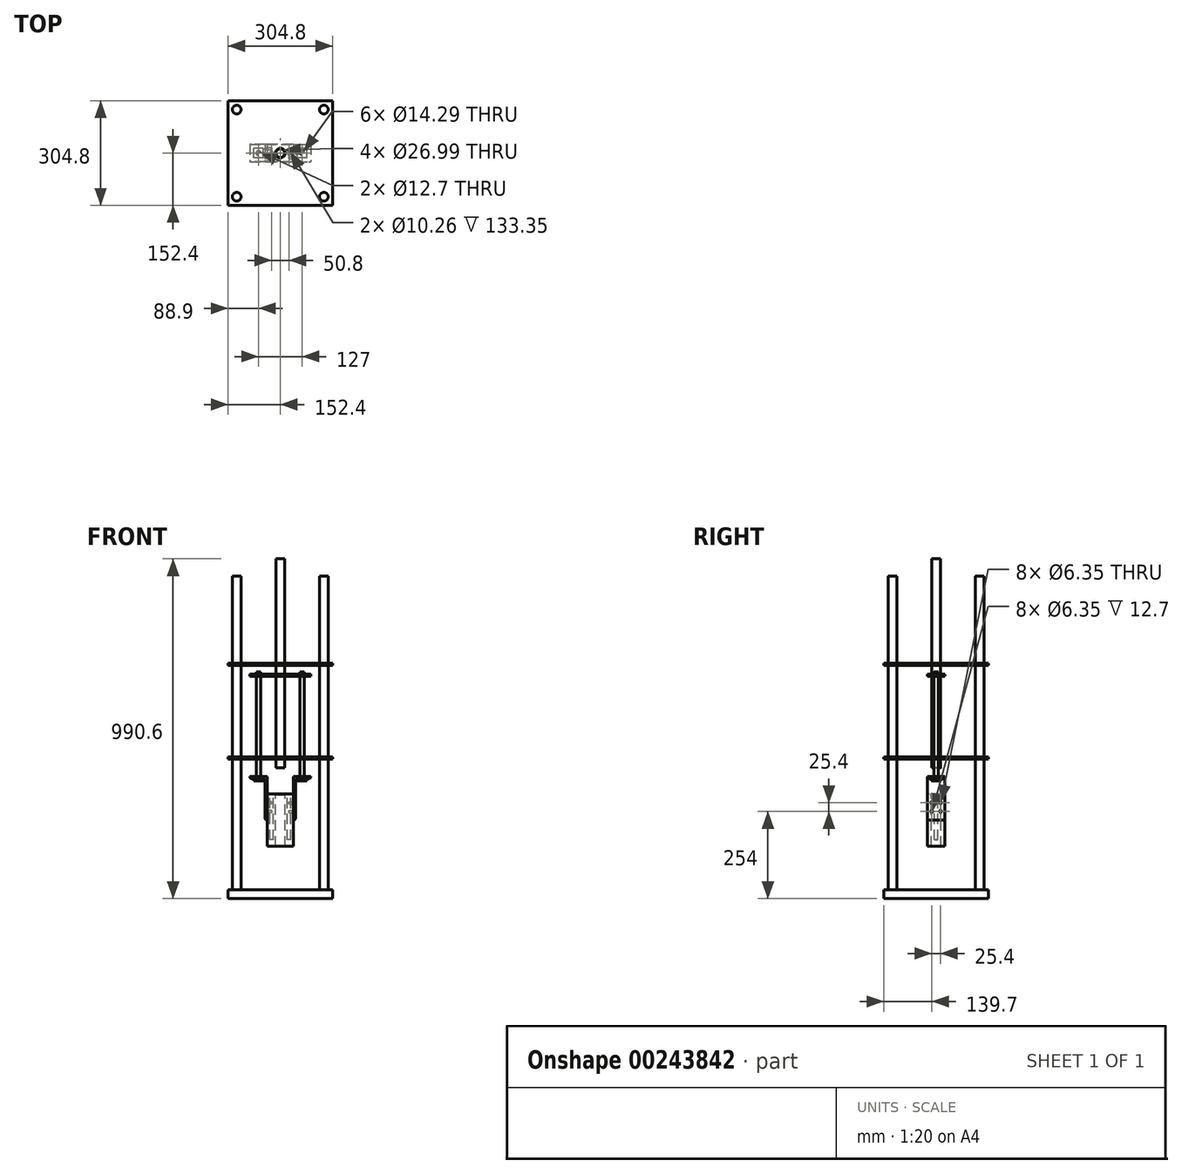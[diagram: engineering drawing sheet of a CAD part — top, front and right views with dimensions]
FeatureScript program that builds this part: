
annotation { "Feature Type Name" : "Feature", "Feature Type Description" : "" }
export const myFeature = defineFeature(function(context is Context, id is Id, definition is map)
    precondition{}
    {
        {
            var Q0;
            Q0=qCreatedBy(makeId("Top.planeOp"),FACE);
            var sketch = newSketch(context, id + "F0", { "sketchPlane" : qUnion([Q0])});
            skPoint(sketch, "E0.middle", {"position": v(0, 0) * mm});
            skLineSegment(sketch, "E1.bottom", {"start": v(152.4, 152.4) * mm, "end": v(-152.4, 152.4) * mm});
            skLineSegment(sketch, "E1.top", {"start": v(152.4, -152.4) * mm, "end": v(-152.4, -152.4) * mm});
            skLineSegment(sketch, "E1.left", {"start": v(152.4, 152.4) * mm, "end": v(152.4, -152.4) * mm});
            skLineSegment(sketch, "E1.right", {"start": v(-152.4, 152.4) * mm, "end": v(-152.4, -152.4) * mm});
            skSolve(sketch);
        }
        {
            var Q0;
            Q0 = qSketchRegion(id + "F0", true);
            extrude(context, id + "F1", {"entities" : qUnion([Q0]), "oppositeDirection" : true, "depth" : 25.4 * mm});
        }
        {
            var Q0;
            Q0=makeQuery(id+"F1.opExtrude","CAP_FACE",FACE,{"disambiguationData":[OSD([sQuery(id+"F0.wireOp",EDGE,"E1.bottom"),sQuery(id+"F0.wireOp",EDGE,"E1.top"),sQuery(id+"F0.wireOp",EDGE,"E1.left"),sQuery(id+"F0.wireOp",EDGE,"E1.right")])],"isStart":true});
            var sketch = newSketch(context, id + "F2", { "sketchPlane" : qUnion([Q0])});
            skLineSegment(sketch, "E2", {"start": v(0, 0) * mm, "end": v(0, 210) * mm});
            skLineSegment(sketch, "E3", {"start": v(0, 0) * mm, "end": v(-229.12, 0) * mm});
            skCircle(sketch, "E4", {"center": v(-127, 127) * mm, "radius": 12.7 * mm});
            skCircle(sketch, "E5.MirrorC", {"center": v(127, 127) * mm, "radius": 12.7 * mm});
            skCircle(sketch, "E6.MirrorC", {"center": v(-127, -127) * mm, "radius": 12.7 * mm});
            skCircle(sketch, "E7.MirrorC", {"center": v(127, -127) * mm, "radius": 12.7 * mm});
            skSolve(sketch);
        }
        {
            var Q0;
            Q0 = qSketchRegion(id + "F2", true);
            extrude(context, id + "F3", {"entities" : qUnion([Q0]), "operationType" : NewBodyOperationType.ADD, "depth" : 914.4 * mm});
        }
        {
            var Q0;
            Q0=makeQuery(id+"F1.opExtrude","CAP_FACE",FACE,{"disambiguationData":[OSD([sQuery(id+"F0.wireOp",EDGE,"E1.bottom"),sQuery(id+"F0.wireOp",EDGE,"E1.top"),sQuery(id+"F0.wireOp",EDGE,"E1.left"),sQuery(id+"F0.wireOp",EDGE,"E1.right")])],"isStart":true});
            cPlane(context, id + "F4", {"entities" : qUnion([Q0]), "cplaneType" : CPlaneType.OFFSET, "offset" : 381 * mm, "width" : 152.4 * mm, "height" : 152.4 * mm});
        }
        {
            var Q0;
            Q0=qCreatedBy(id+"F4.planeOp",FACE);
            var sketch = newSketch(context, id + "F5", { "sketchPlane" : qUnion([Q0])});
            skLineSegment(sketch, "E8", {"start": v(0, 0) * mm, "end": v(0, 75.3) * mm});
            skLineSegment(sketch, "E9", {"start": v(0, 0) * mm, "end": v(-229.12, 0) * mm});
            skCircle(sketch, "E10", {"center": v(-127, 127) * mm, "radius": 12.7 * mm});
            skCircle(sketch, "E11.MirrorC", {"center": v(127, 127) * mm, "radius": 12.7 * mm});
            skCircle(sketch, "E12.MirrorC", {"center": v(-127, -127) * mm, "radius": 12.7 * mm});
            skCircle(sketch, "E13.MirrorC", {"center": v(127, -127) * mm, "radius": 12.7 * mm});
            skLineSegment(sketch, "E14.bottom", {"start": v(152.4, 152.4) * mm, "end": v(-152.4, 152.4) * mm});
            skLineSegment(sketch, "E14.top", {"start": v(152.4, -152.4) * mm, "end": v(-152.4, -152.4) * mm});
            skLineSegment(sketch, "E14.left", {"start": v(152.4, 152.4) * mm, "end": v(152.4, -152.4) * mm});
            skLineSegment(sketch, "E14.right", {"start": v(-152.4, 152.4) * mm, "end": v(-152.4, -152.4) * mm});
            skPoint(sketch, "E14.middle", {"position": v(0, 0) * mm});
            skCircle(sketch, "E15", {"center": v(0, 0) * mm, "radius": 13.5 * mm});
            skCircle(sketch, "E16", {"center": v(63.5, 0) * mm, "radius": 7.14 * mm});
            skCircle(sketch, "E17.MirrorC", {"center": v(-63.5, 0) * mm, "radius": 7.14 * mm});
            skSolve(sketch);
        }
        {
            var Q0;
            Q0 = qSketchRegion(id + "F5", true);
            extrude(context, id + "F6", {"entities" : qUnion([Q0]), "operationType" : NewBodyOperationType.ADD, "depth" : 6.35 * mm});
        }
        {
            var Q0;
            Q0=qCreatedBy(id+"F4.planeOp",FACE);
            cPlane(context, id + "F7", {"entities" : qUnion([Q0]), "cplaneType" : CPlaneType.OFFSET, "offset" : 101.6 * mm, "oppositeDirection" : true, "width" : 152.4 * mm, "height" : 152.4 * mm});
        }
        {
            var Q0;
            Q0=qCreatedBy(id+"F7.planeOp",FACE);
            var sketch = newSketch(context, id + "F8", { "sketchPlane" : qUnion([Q0])});
            skLineSegment(sketch, "E18.bottom", {"start": v(38.1, 25.4) * mm, "end": v(-38.1, 25.4) * mm});
            skLineSegment(sketch, "E18.top", {"start": v(38.1, -25.4) * mm, "end": v(-38.1, -25.4) * mm});
            skLineSegment(sketch, "E18.left", {"start": v(38.1, 25.4) * mm, "end": v(38.1, -25.4) * mm});
            skLineSegment(sketch, "E18.right", {"start": v(-38.1, 25.4) * mm, "end": v(-38.1, -25.4) * mm});
            skPoint(sketch, "E18.middle", {"position": v(0, 0) * mm});
            skCircle(sketch, "E19", {"center": v(0, 0) * mm, "radius": 13.5 * mm});
            skSolve(sketch);
        }
        {
            var Q0;
            Q0 = qSketchRegion(id + "F8", true);
            extrude(context, id + "F9", {"entities" : qUnion([Q0]), "oppositeDirection" : true, "depth" : 152.4 * mm});
        }
        {
            var Q0;
            Q0=makeQuery(id+"F9.opExtrude","CAP_FACE",FACE,{"disambiguationData":[OSD([sQuery(id+"F8.wireOp",EDGE,"E18.bottom"),sQuery(id+"F8.wireOp",EDGE,"E18.top"),sQuery(id+"F8.wireOp",EDGE,"E18.left"),sQuery(id+"F8.wireOp",EDGE,"E18.right"),sQuery(id+"F8.wireOp",EDGE,"E19")])],"isStart":true});
            var sketch = newSketch(context, id + "F10", { "sketchPlane" : qUnion([Q0])});
            skCircle(sketch, "E20", {"center": v(-25.4, 0) * mm, "radius": 5.13 * mm});
            skLineSegment(sketch, "E21", {"start": v(0, 0) * mm, "end": v(0, -39.13) * mm});
            skCircle(sketch, "E22.MirrorC", {"center": v(25.4, 0) * mm, "radius": 5.13 * mm});
            skSolve(sketch);
        }
        {
            var Q0;
            Q0 = qSketchRegion(id + "F10", true);
            extrude(context, id + "F11", {"entities" : qUnion([Q0]), "operationType" : NewBodyOperationType.REMOVE, "oppositeDirection" : true, "depth" : 133.35 * mm});
        }
        {
            var Q0;
            Q0=makeQuery(id+"F9.opExtrude","SWEPT_FACE",FACE,{"disambiguationData":[OSD([sQuery(id+"F8.wireOp",EDGE,"E18.right")])]});
            var sketch = newSketch(context, id + "F12", { "sketchPlane" : qUnion([Q0])});
            skCircle(sketch, "E23", {"center": v(-12.7, 254) * mm, "radius": 3.18 * mm});
            skCircle(sketch, "E24", {"center": v(-12.7, 228.6) * mm, "radius": 3.18 * mm});
            skLineSegment(sketch, "E25", {"start": v(0, 279.4) * mm, "end": v(0, 224) * mm});
            skPoint(sketch, "E25.endSnap0", {"position": v(0, 279.4) * mm});
            skCircle(sketch, "E26.MirrorC", {"center": v(12.7, 228.6) * mm, "radius": 3.18 * mm});
            skCircle(sketch, "E27.MirrorC", {"center": v(12.7, 254) * mm, "radius": 3.18 * mm});
            skSolve(sketch);
        }
        {
            var Q0;
            Q0 = qSketchRegion(id + "F12", true);
            extrude(context, id + "F13", {"entities" : qUnion([Q0]), "operationType" : NewBodyOperationType.REMOVE, "oppositeDirection" : true, "depth" : 12.7 * mm});
        }
        {
            var Q0;
            Q0=makeQuery(id+"F9.opExtrude","SWEPT_FACE",FACE,{"disambiguationData":[OSD([sQuery(id+"F8.wireOp",EDGE,"E18.left")])]});
            var sketch = newSketch(context, id + "F14", { "sketchPlane" : qUnion([Q0])});
            skCircle(sketch, "E28", {"center": v(-12.7, 254) * mm, "radius": 3.18 * mm});
            skCircle(sketch, "E29", {"center": v(-12.7, 228.6) * mm, "radius": 3.18 * mm});
            skLineSegment(sketch, "E30", {"start": v(0, 279.4) * mm, "end": v(0, 198.46) * mm});
            skPoint(sketch, "E30.endSnap0", {"position": v(0, 279.4) * mm});
            skCircle(sketch, "E31.MirrorC", {"center": v(12.7, 228.6) * mm, "radius": 3.18 * mm});
            skCircle(sketch, "E32.MirrorC", {"center": v(12.7, 254) * mm, "radius": 3.18 * mm});
            skSolve(sketch);
        }
        {
            var Q0;
            Q0 = qSketchRegion(id + "F14", true);
            extrude(context, id + "F15", {"entities" : qUnion([Q0]), "operationType" : NewBodyOperationType.REMOVE, "oppositeDirection" : true, "depth" : 12.7 * mm});
        }
        {
            var Q0;
            Q0=makeQuery(id+"F9.opExtrude","SWEPT_FACE",FACE,{"disambiguationData":[OSD([sQuery(id+"F8.wireOp",EDGE,"E18.top")])]});
            var sketch = newSketch(context, id + "F16", { "sketchPlane" : qUnion([Q0])});
            skLineSegment(sketch, "E33", {"start": v(38.1, 330.2) * mm, "end": v(88.9, 330.2) * mm});
            skLineSegment(sketch, "E34", {"start": v(38.1, 330.2) * mm, "end": v(38.1, 203.2) * mm});
            skLineSegment(sketch, "E35.0", {"start": v(44.45, 323.85) * mm, "end": v(82.55, 323.85) * mm});
            skLineSegment(sketch, "E36.0", {"start": v(44.45, 323.85) * mm, "end": v(44.45, 209.55) * mm});
            skArc(sketch, "E37", {"start": v(38.1, 203.2) * mm, "mid": v(42.6, 205.06) * mm, "end": v(44.45, 209.55) * mm});
            skArc(sketch, "E38", {"start": v(82.55, 323.85) * mm, "mid": v(87.04, 325.7) * mm, "end": v(88.9, 330.2) * mm});
            skPoint(sketch, "E39.endSnap0", {"position": v(0, 279.4) * mm});
            skLineSegment(sketch, "E40.MirrorCS", {"start": v(-44.45, 323.85) * mm, "end": v(-44.45, 209.55) * mm});
            skLineSegment(sketch, "E41.MirrorCS", {"start": v(-38.1, 330.2) * mm, "end": v(-38.1, 203.2) * mm});
            skArc(sketch, "E42.MirrorCS", {"start": v(-38.1, 203.2) * mm, "mid": v(-42.6, 205.06) * mm, "end": v(-44.45, 209.55) * mm});
            skArc(sketch, "E43.MirrorCS", {"start": v(-82.55, 323.85) * mm, "mid": v(-87.04, 325.7) * mm, "end": v(-88.9, 330.2) * mm});
            skLineSegment(sketch, "E44.MirrorCS", {"start": v(-44.45, 323.85) * mm, "end": v(-82.55, 323.85) * mm});
            skLineSegment(sketch, "E45.MirrorCS", {"start": v(-38.1, 330.2) * mm, "end": v(-88.9, 330.2) * mm});
            skLineSegment(sketch, "E46", {"start": v(0, 279.4) * mm, "end": v(0, 330.2) * mm});
            skLineSegment(sketch, "E47", {"start": v(0, 330.2) * mm, "end": v(38.1, 330.2) * mm});
            skLineSegment(sketch, "E48", {"start": v(0, 330.2) * mm, "end": v(-38.1, 330.2) * mm});
            skSolve(sketch);
        }
        {
            var Q0;
            Q0 = qSketchRegion(id + "F16", true);
            extrude(context, id + "F17", {"entities" : qUnion([Q0]), "oppositeDirection" : true, "depth" : 50.8 * mm});
        }
        {
            var Q0;
            Q0=makeQuery(id+"F17.opExtrude","SWEPT_FACE",FACE,{"disambiguationData":[OSD([sQuery(id+"F16.wireOp",EDGE,"E36.0")])]});
            var sketch = newSketch(context, id + "F18", { "sketchPlane" : qUnion([Q0])});
            skCircle(sketch, "E49", {"center": v(-12.7, 254) * mm, "radius": 3.18 * mm});
            skCircle(sketch, "E50", {"center": v(-12.7, 228.6) * mm, "radius": 3.18 * mm});
            skLineSegment(sketch, "E51", {"start": v(0, 279.4) * mm, "end": v(0, 194.62) * mm});
            skPoint(sketch, "E51.endSnap0", {"position": v(0, 279.4) * mm});
            skCircle(sketch, "E52.MirrorC", {"center": v(12.7, 228.6) * mm, "radius": 3.18 * mm});
            skCircle(sketch, "E53.MirrorC", {"center": v(12.7, 254) * mm, "radius": 3.18 * mm});
            skPoint(sketch, "E54", {"position": v(0, 323.85) * mm});
            skSolve(sketch);
        }
        {
            var Q0;
            Q0 = qSketchRegion(id + "F18", true);
            extrude(context, id + "F19", {"entities" : qUnion([Q0]), "operationType" : NewBodyOperationType.REMOVE, "oppositeDirection" : true, "depth" : 6.35 * mm});
        }
        {
            var Q0;
            Q0=makeQuery(id+"F17.opExtrude","SWEPT_FACE",FACE,{"disambiguationData":[OSD([sQuery(id+"F16.wireOp",EDGE,"E40.MirrorCS")])]});
            var sketch = newSketch(context, id + "F20", { "sketchPlane" : qUnion([Q0])});
            skCircle(sketch, "E55", {"center": v(-12.7, 254) * mm, "radius": 3.18 * mm});
            skCircle(sketch, "E56", {"center": v(-12.7, 228.6) * mm, "radius": 3.18 * mm});
            skLineSegment(sketch, "E57", {"start": v(0, 279.4) * mm, "end": v(0, 194.62) * mm});
            skPoint(sketch, "E57.endSnap0", {"position": v(0, 279.4) * mm});
            skCircle(sketch, "E58.MirrorC", {"center": v(12.7, 228.6) * mm, "radius": 3.18 * mm});
            skCircle(sketch, "E59.MirrorC", {"center": v(12.7, 254) * mm, "radius": 3.18 * mm});
            skSolve(sketch);
        }
        {
            var Q0;
            Q0 = qSketchRegion(id + "F20", true);
            extrude(context, id + "F21", {"entities" : qUnion([Q0]), "operationType" : NewBodyOperationType.REMOVE, "oppositeDirection" : true, "depth" : 6.35 * mm});
        }
        {
            var Q0;
            Q0=makeQuery(id+"F17.opExtrude","SWEPT_FACE",FACE,{"disambiguationData":[OSD([sQuery(id+"F16.wireOp",EDGE,"E33")])]});
            var sketch = newSketch(context, id + "F22", { "sketchPlane" : qUnion([Q0])});
            skCircle(sketch, "E60", {"center": v(63.5, 0) * mm, "radius": 6.35 * mm});
            skPoint(sketch, "E60.centerSnap0", {"position": v(63.5, -25.4) * mm});
            skPoint(sketch, "E60.centerSnap1", {"position": v(88.9, 0) * mm});
            skLineSegment(sketch, "E61", {"start": v(0, 0) * mm, "end": v(0, -38.93) * mm});
            skCircle(sketch, "E62.MirrorC", {"center": v(-63.5, 0) * mm, "radius": 6.35 * mm});
            skSolve(sketch);
        }
        {
            var Q0;
            Q0 = qSketchRegion(id + "F22", true);
            extrude(context, id + "F23", {"entities" : qUnion([Q0]), "operationType" : NewBodyOperationType.REMOVE, "oppositeDirection" : true, "depth" : 6.35 * mm});
        }
        {
            var Q0;
            Q0=makeQuery(id+"F17.opExtrude","SWEPT_FACE",FACE,{"disambiguationData":[OSD([sQuery(id+"F16.wireOp",EDGE,"E33")])]});
            var sketch = newSketch(context, id + "F24", { "sketchPlane" : qUnion([Q0])});
            skCircle(sketch, "E63", {"center": v(63.5, 0) * mm, "radius": 6.35 * mm});
            skLineSegment(sketch, "E64", {"start": v(0, 0) * mm, "end": v(0, -44.9) * mm});
            skCircle(sketch, "E65.MirrorC", {"center": v(-63.5, 0) * mm, "radius": 6.35 * mm});
            skSolve(sketch);
        }
        {
            var Q0;
            Q0 = qSketchRegion(id + "F24", true);
            extrude(context, id + "F25", {"entities" : qUnion([Q0]), "depth" : 304.8 * mm, "hasSecondDirection" : true, "secondDirectionOppositeDirection" : true, "secondDirectionDepth" : 12.7 * mm});
        }
        {
            var Q0;
            Q0=makeQuery(id+"F6.opExtrude","CAP_FACE",FACE,{"disambiguationData":[OSD([sQuery(id+"F5.wireOp",EDGE,"E10"),sQuery(id+"F5.wireOp",EDGE,"E11.MirrorC"),sQuery(id+"F5.wireOp",EDGE,"E12.MirrorC"),sQuery(id+"F5.wireOp",EDGE,"E13.MirrorC"),sQuery(id+"F5.wireOp",EDGE,"E14.bottom"),sQuery(id+"F5.wireOp",EDGE,"E14.top"),sQuery(id+"F5.wireOp",EDGE,"E14.left"),sQuery(id+"F5.wireOp",EDGE,"E14.right"),sQuery(id+"F5.wireOp",EDGE,"E15"),sQuery(id+"F5.wireOp",EDGE,"E16"),sQuery(id+"F5.wireOp",EDGE,"E17.MirrorC")])],"isStart":false});
            cPlane(context, id + "F26", {"entities" : qUnion([Q0]), "cplaneType" : CPlaneType.OFFSET, "offset" : 234.95 * mm, "width" : 152.4 * mm, "height" : 152.4 * mm});
        }
        {
            var Q0;
            Q0=qCreatedBy(id+"F26.planeOp",FACE);
            var sketch = newSketch(context, id + "F27", { "sketchPlane" : qUnion([Q0])});
            skLineSegment(sketch, "E66.bottom", {"start": v(-88.9, 25.4) * mm, "end": v(88.9, 25.4) * mm});
            skLineSegment(sketch, "E66.top", {"start": v(-88.9, -25.4) * mm, "end": v(88.9, -25.4) * mm});
            skLineSegment(sketch, "E66.left", {"start": v(-88.9, 25.4) * mm, "end": v(-88.9, -25.4) * mm});
            skLineSegment(sketch, "E66.right", {"start": v(88.9, 25.4) * mm, "end": v(88.9, -25.4) * mm});
            skPoint(sketch, "E66.middle", {"position": v(0, 0) * mm});
            skCircle(sketch, "E67", {"center": v(0, 0) * mm, "radius": 13.5 * mm});
            skCircle(sketch, "E68", {"center": v(-63.5, 0) * mm, "radius": 7.14 * mm});
            skCircle(sketch, "E69", {"center": v(63.5, 0) * mm, "radius": 7.14 * mm});
            skSolve(sketch);
        }
        {
            var Q0;
            Q0 = qSketchRegion(id + "F27", true);
            extrude(context, id + "F28", {"entities" : qUnion([Q0]), "depth" : 6.35 * mm});
        }
        {
            var Q0;
            Q0=makeQuery(id+"F9.opExtrude","CAP_EDGE",EDGE,{"disambiguationData":[OSD([sQuery(id+"F8.wireOp",EDGE,"E19")])],"isStart":true});
            chamfer(context, id + "F29", {"entities" : qUnion([Q0]), "width" : 3.17 * mm, "tangentPropagation" : true});
        }
        {
            var Q0;
            Q0=makeQuery(id+"F6.opExtrude","CAP_EDGE",EDGE,{"disambiguationData":[OSD([sQuery(id+"F5.wireOp",EDGE,"E15")])],"isStart":false});
            chamfer(context, id + "F30", {"entities" : qUnion([Q0]), "width" : 3.17 * mm, "tangentPropagation" : true});
        }
        {
            var Q0;
            Q0=makeQuery(id+"F28.opExtrude","CAP_FACE",FACE,{"disambiguationData":[OSD([sQuery(id+"F27.wireOp",EDGE,"E66.bottom"),sQuery(id+"F27.wireOp",EDGE,"E66.top"),sQuery(id+"F27.wireOp",EDGE,"E66.left"),sQuery(id+"F27.wireOp",EDGE,"E66.right"),sQuery(id+"F27.wireOp",EDGE,"E67"),sQuery(id+"F27.wireOp",EDGE,"E68"),sQuery(id+"F27.wireOp",EDGE,"E69")])],"isStart":false});
            cPlane(context, id + "F31", {"entities" : qUnion([Q0]), "cplaneType" : CPlaneType.OFFSET, "offset" : 25.4 * mm, "width" : 152.4 * mm, "height" : 152.4 * mm});
        }
        {
            var Q0;
            Q0=qCreatedBy(id+"F31.planeOp",FACE);
            var sketch = newSketch(context, id + "F32", { "sketchPlane" : qUnion([Q0])});
            skLineSegment(sketch, "E70", {"start": v(0, 0) * mm, "end": v(0, 59.47) * mm});
            skLineSegment(sketch, "E71", {"start": v(0, 0) * mm, "end": v(-229.12, 0) * mm});
            skCircle(sketch, "E72", {"center": v(-127, 127) * mm, "radius": 12.7 * mm});
            skCircle(sketch, "E73.MirrorC", {"center": v(127, 127) * mm, "radius": 12.7 * mm});
            skCircle(sketch, "E74.MirrorC", {"center": v(-127, -127) * mm, "radius": 12.7 * mm});
            skCircle(sketch, "E75.MirrorC", {"center": v(127, -127) * mm, "radius": 12.7 * mm});
            skLineSegment(sketch, "E76.bottom", {"start": v(152.4, 152.4) * mm, "end": v(-152.4, 152.4) * mm});
            skLineSegment(sketch, "E76.top", {"start": v(152.4, -152.4) * mm, "end": v(-152.4, -152.4) * mm});
            skLineSegment(sketch, "E76.left", {"start": v(152.4, 152.4) * mm, "end": v(152.4, -152.4) * mm});
            skLineSegment(sketch, "E76.right", {"start": v(-152.4, 152.4) * mm, "end": v(-152.4, -152.4) * mm});
            skPoint(sketch, "E76.middle", {"position": v(0, 0) * mm});
            skCircle(sketch, "E77", {"center": v(0, 0) * mm, "radius": 13.5 * mm});
            skSolve(sketch);
        }
        {
            var Q0;
            Q0=makeQuery(id+"F32.imprint","IMPRINT",FACE,{"disambiguationData":[TD([[makeQuery(id+"F32.imprint","IMPRINT",EDGE,{"derivedFrom":sQuery(id+"F32.wireOp",EDGE,"E72")}),-1.0]])]});
            extrude(context, id + "F33", {"entities" : qUnion([Q0]), "operationType" : NewBodyOperationType.ADD, "depth" : 6.35 * mm});
        }
        {
            var Q0;
            Q0=makeQuery(id+"F25.opExtrude","CAP_FACE",FACE,{"disambiguationData":[OSD([sQuery(id+"F24.wireOp",EDGE,"E63")])],"isStart":true});
            var sketch = newSketch(context, id + "F34", { "sketchPlane" : qUnion([Q0])});
            skLineSegment(sketch, "E78.bottom", {"start": v(77.79, 14.29) * mm, "end": v(49.21, 14.29) * mm});
            skLineSegment(sketch, "E78.top", {"start": v(77.79, -14.29) * mm, "end": v(49.21, -14.29) * mm});
            skLineSegment(sketch, "E78.left", {"start": v(77.79, 14.29) * mm, "end": v(77.79, -14.29) * mm});
            skLineSegment(sketch, "E78.right", {"start": v(49.21, 14.29) * mm, "end": v(49.21, -14.29) * mm});
            skPoint(sketch, "E78.middle", {"position": v(63.5, 0) * mm});
            skCircle(sketch, "E79", {"center": v(63.5, 0) * mm, "radius": 7.14 * mm});
            skSolve(sketch);
        }
        {
            var Q0;
            Q0 = qSketchRegion(id + "F34", true);
            extrude(context, id + "F35", {"entities" : qUnion([Q0]), "oppositeDirection" : true, "depth" : 6.35 * mm});
        }
        {
            var Q0;
            Q0=makeQuery(id+"F25.opExtrude","CAP_FACE",FACE,{"disambiguationData":[OSD([sQuery(id+"F24.wireOp",EDGE,"E65.MirrorC")])],"isStart":true});
            var sketch = newSketch(context, id + "F36", { "sketchPlane" : qUnion([Q0])});
            skLineSegment(sketch, "E80.bottom", {"start": v(-49.21, 14.29) * mm, "end": v(-77.79, 14.29) * mm});
            skLineSegment(sketch, "E80.top", {"start": v(-49.21, -14.29) * mm, "end": v(-77.79, -14.29) * mm});
            skLineSegment(sketch, "E80.left", {"start": v(-49.21, 14.29) * mm, "end": v(-49.21, -14.29) * mm});
            skLineSegment(sketch, "E80.right", {"start": v(-77.79, 14.29) * mm, "end": v(-77.79, -14.29) * mm});
            skPoint(sketch, "E80.middle", {"position": v(-63.5, 0) * mm});
            skCircle(sketch, "E81", {"center": v(-63.5, 0) * mm, "radius": 7.14 * mm});
            skSolve(sketch);
        }
        {
            var Q0;
            Q0=makeQuery(id+"F36.imprint","IMPRINT",FACE,{"disambiguationData":[TD([[makeQuery(id+"F36.imprint","IMPRINT",EDGE,{"derivedFrom":sQuery(id+"F36.wireOp",EDGE,"E80.bottom")}),1.0]])]});
            extrude(context, id + "F37", {"entities" : qUnion([Q0]), "oppositeDirection" : true, "depth" : 6.35 * mm});
        }
        {
            var Q0;
            Q0=qCreatedBy(id+"F4.planeOp",FACE);
            cPlane(context, id + "F38", {"entities" : qUnion([Q0]), "cplaneType" : CPlaneType.OFFSET, "offset" : 25.4 * mm, "oppositeDirection" : true, "width" : 152.4 * mm, "height" : 152.4 * mm});
        }
        {
            var Q0;
            Q0=qCreatedBy(id+"F38.planeOp",FACE);
            var sketch = newSketch(context, id + "F39", { "sketchPlane" : qUnion([Q0])});
            skCircle(sketch, "E82", {"center": v(0, 0) * mm, "radius": 12.7 * mm});
            skSolve(sketch);
        }
        {
            var Q0;
            Q0 = qSketchRegion(id + "F39", true);
            extrude(context, id + "F40", {"entities" : qUnion([Q0]), "depth" : 609.6 * mm});
        }
    });
